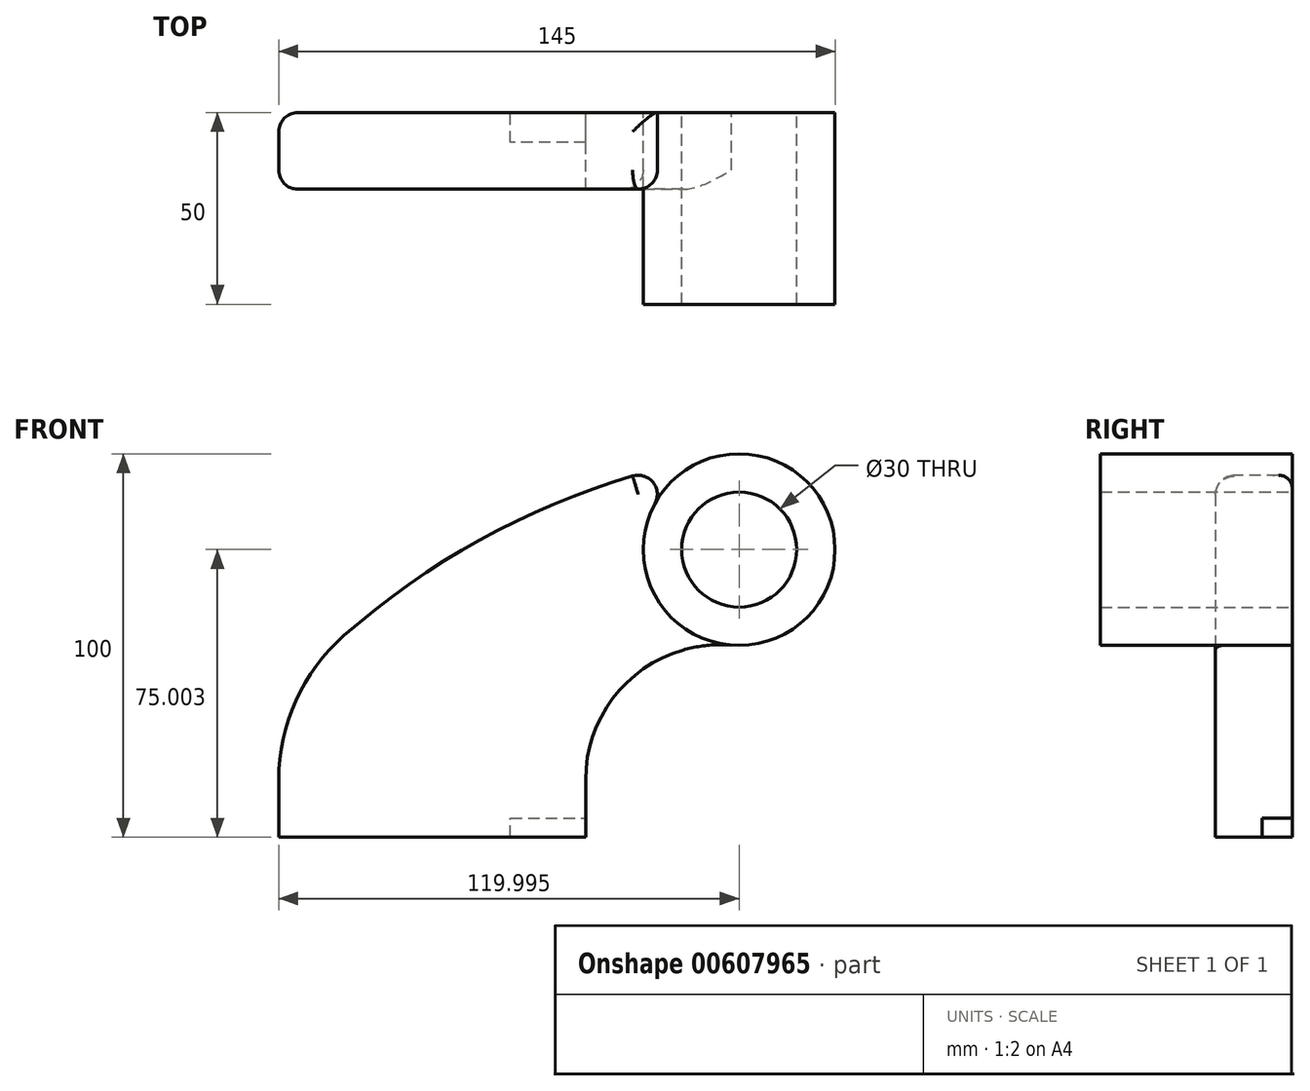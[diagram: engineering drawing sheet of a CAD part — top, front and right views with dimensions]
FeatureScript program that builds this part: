
annotation { "Feature Type Name" : "Feature", "Feature Type Description" : "" }
export const myFeature = defineFeature(function(context is Context, id is Id, definition is map)
    precondition{}
    {
        {
            var Q0;
            Q0=qCreatedBy(makeId("Front.planeOp"),FACE);
            var sketch = newSketch(context, id + "F0", { "sketchPlane" : qUnion([Q0])});
            skLineSegment(sketch, "E0.bottom", {"start": v(-60.38, -15.87) * mm, "end": v(19.62, -15.87) * mm});
            skLineSegment(sketch, "E0.top", {"start": v(-60.38, -30.87) * mm, "end": v(19.62, -30.87) * mm});
            skLineSegment(sketch, "E0.left", {"start": v(-60.38, -15.87) * mm, "end": v(-60.38, -30.87) * mm});
            skLineSegment(sketch, "E0.right", {"start": v(19.62, -15.87) * mm, "end": v(19.62, -30.87) * mm});
            skLineSegment(sketch, "E1", {"start": v(-60.55, -55.87) * mm, "end": v(19.62, -55.87) * mm, "construction": true});
            skCircle(sketch, "E2", {"center": v(59.62, 44.13) * mm, "radius": 15 * mm});
            skCircle(sketch, "E3", {"center": v(59.62, 44.13) * mm, "radius": 25 * mm});
            skArc(sketch, "E4", {"start": v(57.62, 19.21) * mm, "mid": v(30.94, 10) * mm, "end": v(19.62, -15.87) * mm});
            skArc(sketch, "E5", {"start": v(-43.44, 21.65) * mm, "mid": v(-55.95, 4.72) * mm, "end": v(-60.38, -15.87) * mm});
            skArc(sketch, "E6", {"start": v(55.45, 68.78) * mm, "mid": v(2.72, 52.12) * mm, "end": v(-43.44, 21.65) * mm});
            skSolve(sketch);
        }
        {
            var Q0;
            Q0=makeQuery(id+"F0.imprint","IMPRINT",FACE,{"disambiguationData":[TD([[makeQuery(id+"F0.imprint","IMPRINT",EDGE,{"derivedFrom":sQuery(id+"F0.wireOp",EDGE,"E0.bottom")}),1.0]])]});
            var Q1;
            Q1=makeQuery(id+"F0.imprint","IMPRINT",FACE,{"disambiguationData":[TD([[makeQuery(id+"F0.imprint","IMPRINT",EDGE,{"derivedFrom":sQuery(id+"F0.wireOp",EDGE,"E0.bottom")}),-1.0]])]});
            extrude(context, id + "F1", {"entities" : qUnion([Q0, Q1]), "depth" : 20 * mm, "offsetDistance" : 25 * mm});
        }
        {
            var Q0;
            Q0=makeQuery(id+"F0.imprint","IMPRINT",FACE,{"disambiguationData":[TD([[makeQuery(id+"F0.imprint","IMPRINT",EDGE,{"derivedFrom":sQuery(id+"F0.wireOp",EDGE,"E2")}),-1.0]])]});
            extrude(context, id + "F2", {"entities" : qUnion([Q0]), "depth" : 50 * mm, "offsetDistance" : 25 * mm});
        }
        {
            var Q0;
            Q0=makeQuery(id+"F1.opExtrude","CAP_EDGE",EDGE,{"disambiguationData":[OSD([sQuery(id+"F0.wireOp",EDGE,"E5")])],"isStart":false});
            fillet(context, id + "F3", {"entities" : qUnion([Q0]), "radius" : 5 * mm, "tangentPropagation" : true, "allowEdgeOverflow" : false});
        }
        {
            var Q0;
            Q0=makeQuery(id+"F1.opExtrude","SWEPT_FACE",FACE,{"disambiguationData":[OSD([sQuery(id+"F0.wireOp",EDGE,"E6")])]});
            var Q1;
            Q1=makeQuery(id+"F3.opFillet","BLEND_EDGE",EDGE,{"blendedFrom":[makeQuery(id+"F1.opExtrude","CAP_EDGE",EDGE,{"disambiguationData":[OSD([sQuery(id+"F0.wireOp",EDGE,"E6")])],"isStart":false}),makeQuery(id+"F1.opExtrude","SWEPT_FACE",FACE,{"disambiguationData":[OSD([sQuery(id+"F0.wireOp",EDGE,"E3")])]})],"blendedInto":[makeQuery(id+"F1.opExtrude","SWEPT_FACE",FACE,{"disambiguationData":[OSD([sQuery(id+"F0.wireOp",EDGE,"E3")])]})]});
            var Q2;
            {var subQ0=sQuery(id+"F0.wireOp",EDGE,"E6");Q2=makeQuery(id+"F3.opFillet","BLEND_EDGE",EDGE,{"blendedFrom":[makeQuery(id+"F1.opExtrude","CAP_EDGE",EDGE,{"disambiguationData":[OSD([subQ0])],"isStart":false}),makeQuery(id+"F1.opExtrude","CAP_FACE",FACE,{"disambiguationData":[OSD([sQuery(id+"F0.wireOp",EDGE,"E0.top"),sQuery(id+"F0.wireOp",EDGE,"E0.left"),sQuery(id+"F0.wireOp",EDGE,"E0.right"),sQuery(id+"F0.wireOp",EDGE,"E3"),sQuery(id+"F0.wireOp",EDGE,"E4"),sQuery(id+"F0.wireOp",EDGE,"E5"),subQ0])],"isStart":false})],"blendedInto":[makeQuery(id+"F1.opExtrude","CAP_FACE",FACE,{"disambiguationData":[OSD([sQuery(id+"F0.wireOp",EDGE,"E0.top"),sQuery(id+"F0.wireOp",EDGE,"E0.left"),sQuery(id+"F0.wireOp",EDGE,"E0.right"),sQuery(id+"F0.wireOp",EDGE,"E3"),sQuery(id+"F0.wireOp",EDGE,"E4"),sQuery(id+"F0.wireOp",EDGE,"E5"),subQ0])],"isStart":false})]});}
            var Q3;
            {var subQ0=sQuery(id+"F0.wireOp",EDGE,"E5");Q3=makeQuery(id+"F3.opFillet","BLEND_EDGE",EDGE,{"blendedFrom":[makeQuery(id+"F1.opExtrude","CAP_EDGE",EDGE,{"disambiguationData":[OSD([subQ0])],"isStart":false}),makeQuery(id+"F1.opExtrude","CAP_FACE",FACE,{"disambiguationData":[OSD([sQuery(id+"F0.wireOp",EDGE,"E0.top"),sQuery(id+"F0.wireOp",EDGE,"E0.left"),sQuery(id+"F0.wireOp",EDGE,"E0.right"),sQuery(id+"F0.wireOp",EDGE,"E3"),sQuery(id+"F0.wireOp",EDGE,"E4"),subQ0,sQuery(id+"F0.wireOp",EDGE,"E6")])],"isStart":false})],"blendedInto":[makeQuery(id+"F1.opExtrude","CAP_FACE",FACE,{"disambiguationData":[OSD([sQuery(id+"F0.wireOp",EDGE,"E0.top"),sQuery(id+"F0.wireOp",EDGE,"E0.left"),sQuery(id+"F0.wireOp",EDGE,"E0.right"),sQuery(id+"F0.wireOp",EDGE,"E3"),sQuery(id+"F0.wireOp",EDGE,"E4"),subQ0,sQuery(id+"F0.wireOp",EDGE,"E6")])],"isStart":false})]});}
            var Q4;
            {var subQ0=sQuery(id+"F0.wireOp",EDGE,"E5");Q4=makeQuery(id+"F3.opFillet","BLEND_EDGE",EDGE,{"blendedFrom":[makeQuery(id+"F1.opExtrude","CAP_EDGE",EDGE,{"disambiguationData":[OSD([subQ0])],"isStart":false}),makeQuery(id+"F1.opExtrude","SWEPT_FACE",FACE,{"disambiguationData":[OSD([subQ0])]})],"blendedInto":[makeQuery(id+"F1.opExtrude","SWEPT_FACE",FACE,{"disambiguationData":[OSD([subQ0])]})]});}
            var Q5;
            Q5=makeQuery(id+"F1.opExtrude","SWEPT_FACE",FACE,{"disambiguationData":[OSD([sQuery(id+"F0.wireOp",EDGE,"E5")])]});
            var Q6;
            Q6=makeQuery(id+"F1.opExtrude","CAP_EDGE",EDGE,{"disambiguationData":[OSD([sQuery(id+"F0.wireOp",EDGE,"E3")])],"isStart":false});
            var Q7;
            {var subQ0=sQuery(id+"F0.wireOp",EDGE,"E6");Q7=makeQuery(id+"F3.opFillet","BLEND_EDGE",EDGE,{"blendedFrom":[makeQuery(id+"F1.opExtrude","CAP_EDGE",EDGE,{"disambiguationData":[OSD([subQ0])],"isStart":false}),makeQuery(id+"F1.opExtrude","SWEPT_FACE",FACE,{"disambiguationData":[OSD([subQ0])]})],"blendedInto":[makeQuery(id+"F1.opExtrude","SWEPT_FACE",FACE,{"disambiguationData":[OSD([subQ0])]})]});}
            var Q8;
            Q8=makeQuery(id+"F1.opExtrude","CAP_EDGE",EDGE,{"disambiguationData":[OSD([sQuery(id+"F0.wireOp",EDGE,"E6")])],"isStart":true});
            fillet(context, id + "F4", {"entities" : qUnion([Q0, Q1, Q2, Q3, Q4, Q5, Q6, Q7, Q8]), "radius" : 5 * mm, "tangentPropagation" : true, "allowEdgeOverflow" : false});
        }
        {
            var Q0;
            Q0=qCreatedBy(makeId("Right.planeOp"),FACE);
            var sketch = newSketch(context, id + "F5", { "sketchPlane" : qUnion([Q0])});
            skLineSegment(sketch, "E7.bottom", {"start": v(6.2, -25.88) * mm, "end": v(-7.8, -25.88) * mm});
            skLineSegment(sketch, "E7.top", {"start": v(6.2, -55.88) * mm, "end": v(-7.8, -55.88) * mm});
            skLineSegment(sketch, "E7.left", {"start": v(6.2, -25.88) * mm, "end": v(6.2, -55.88) * mm});
            skLineSegment(sketch, "E7.right", {"start": v(-7.8, -25.88) * mm, "end": v(-7.8, -55.88) * mm});
            skSolve(sketch);
        }
        {
            var Q0;
            Q0=makeQuery(id+"F5.imprint","IMPRINT",FACE,{"disambiguationData":[TD([[makeQuery(id+"F5.imprint","IMPRINT",EDGE,{"derivedFrom":sQuery(id+"F5.wireOp",EDGE,"E7.bottom")}),1.0]])]});
            extrude(context, id + "F6", {"entities" : qUnion([Q0]), "operationType" : NewBodyOperationType.REMOVE, "depth" : 80 * mm, "offsetDistance" : 25 * mm});
        }
    });
